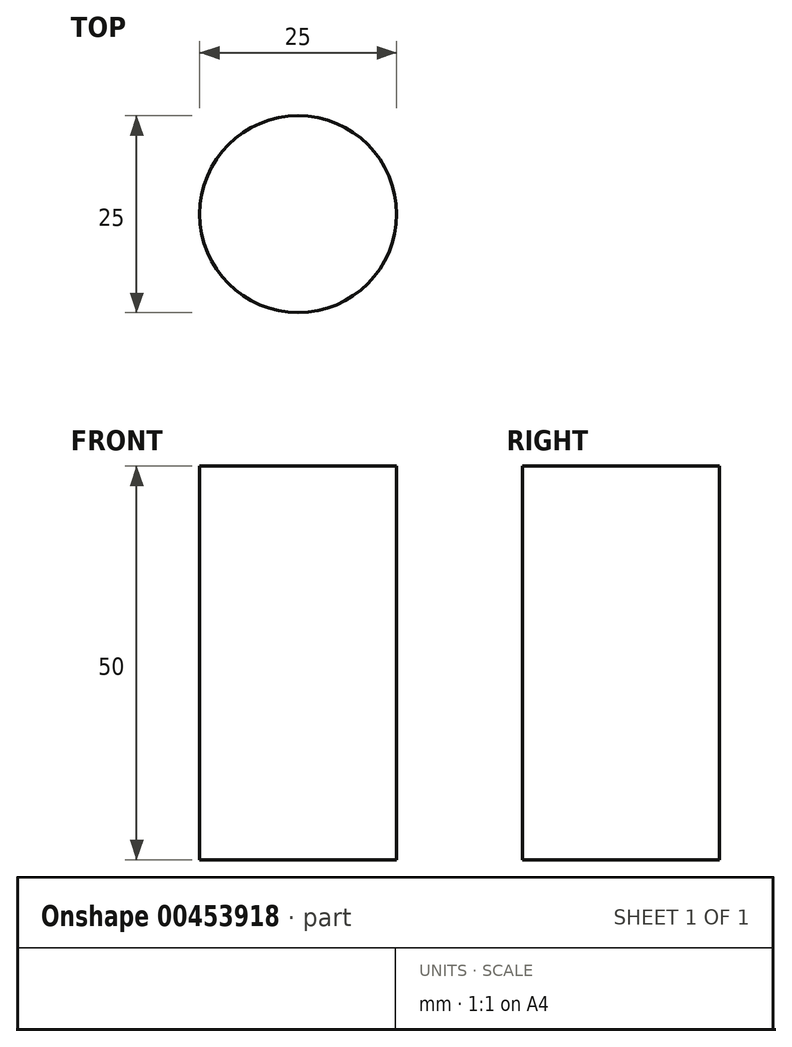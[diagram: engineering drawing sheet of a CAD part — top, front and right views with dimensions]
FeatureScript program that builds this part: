
annotation { "Feature Type Name" : "Feature", "Feature Type Description" : "" }
export const myFeature = defineFeature(function(context is Context, id is Id, definition is map)
    precondition{}
    {
        {
            var Q0;
            Q0=qCreatedBy(makeId("Top.planeOp"),FACE);
            var sketch = newSketch(context, id + "F0", { "sketchPlane" : qUnion([Q0])});
            skCircle(sketch, "E0", {"center": v(0, 0) * mm, "radius": 31.82 * mm});
            skSolve(sketch);
        }
        {
            var Q0;
            Q0=makeQuery(id+"F0.imprint","IMPRINT",FACE,{"disambiguationData":[TD([[makeQuery(id+"F0.imprint","IMPRINT",EDGE,{"derivedFrom":sQuery(id+"F0.wireOp",EDGE,"E0")}),1.0]])]});
            var sketch = newSketch(context, id + "F1", { "sketchPlane" : qUnion([Q0])});
            skSolve(sketch);
        }
        {
            var Q0;
            Q0 = qSketchRegion(id + "F1", true);
            var Q1;
            Q1=makeQuery(id+"F0.imprint","IMPRINT",FACE,{"disambiguationData":[TD([[makeQuery(id+"F0.imprint","IMPRINT",EDGE,{"derivedFrom":sQuery(id+"F0.wireOp",EDGE,"E0")}),1.0]])]});
            var Q2;
            Q2=makeQuery(id+"F1.imprint","IMPRINT",FACE,{"disambiguationData":[TD([[makeQuery(id+"F1.imprint","IMPRINT",EDGE,{"derivedFrom":makeQuery(id+"F0.imprint","IMPRINT",EDGE,{"derivedFrom":sQuery(id+"F0.wireOp",EDGE,"E0")})}),1.0]])]});
            extrude(context, id + "F2", {"entities" : qUnion([Q0, Q1, Q2]), "depth" : 50 * mm});
        }
        {
            var Q0;
            {var subQ0=sQuery(id+"F0.wireOp",EDGE,"E0");Q0=makeQuery(id+"F2.opExtrude","CAP_FACE",FACE,{"disambiguationData":[OSD([subQ0]),TDD([makeQuery(id+"F0.imprint","IMPRINT",EDGE,{"derivedFrom":subQ0})])],"isStart":false});}
            var sketch = newSketch(context, id + "F3", { "sketchPlane" : qUnion([Q0])});
            skSolve(sketch);
        }
        {
            var Q0;
            {var subQ0=sQuery(id+"F0.wireOp",EDGE,"E0");Q0=makeQuery(id+"F3.imprint","IMPRINT",FACE,{"disambiguationData":[TD([[makeQuery(id+"F3.imprint","IMPRINT",EDGE,{"derivedFrom":makeQuery(id+"F2.opExtrude","CAP_EDGE",EDGE,{"disambiguationData":[OSD([subQ0]),TDD([makeQuery(id+"F0.imprint","IMPRINT",EDGE,{"derivedFrom":subQ0})])],"isStart":false})}),1.0]])]});}
            var sketch = newSketch(context, id + "F4", { "sketchPlane" : qUnion([Q0])});
            skCircle(sketch, "E1", {"center": v(0, 0) * mm, "radius": 12.5 * mm});
            skSolve(sketch);
        }
        {
            var Q0;
            Q0=makeQuery(id+"F4.imprint","IMPRINT",FACE,{"disambiguationData":[TD([[makeQuery(id+"F4.imprint","IMPRINT",EDGE,{"derivedFrom":sQuery(id+"F4.wireOp",EDGE,"E1")}),-1.0]])]});
            var Q1;
            Q1=sQuery(id+"F4.wireOp",EDGE,"E1");
            extrude(context, id + "F5", {"entities" : qUnion([Q0]), "operationType" : NewBodyOperationType.REMOVE, "surfaceEntities" : qUnion([Q1]), "oppositeDirection" : true, "depth" : 100 * mm});
        }
    });
